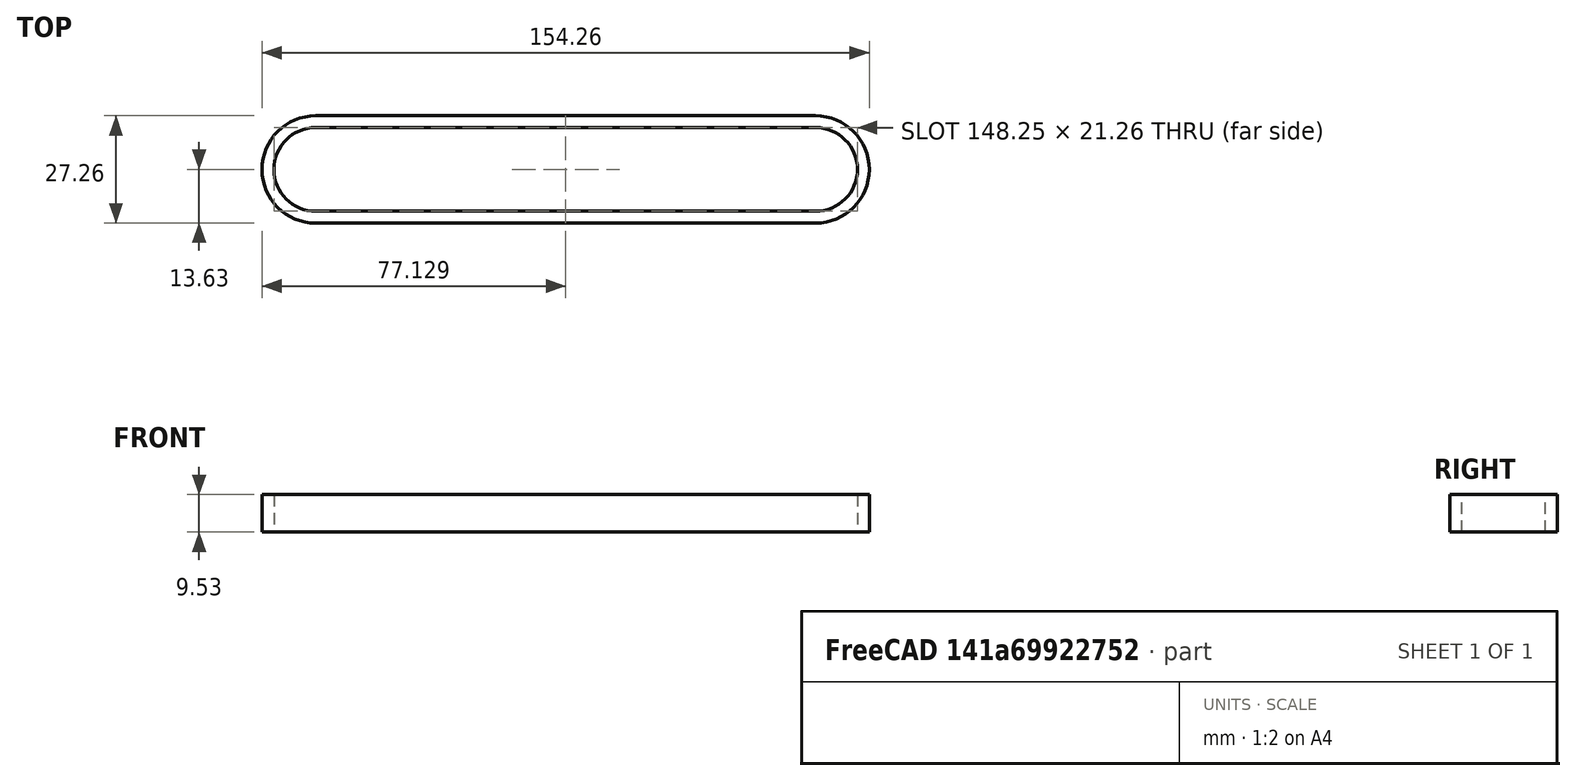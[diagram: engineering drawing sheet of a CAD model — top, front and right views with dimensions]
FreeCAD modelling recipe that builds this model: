
FCSTD DOCUMENT  (FreeCAD 0.19R22665 (Git))
Label: BELT-XL-130-375
License: All rights reserved
LicenseURL: http://en.wikipedia.org/wiki/All_rights_reserved
objects: Sketcher::SketchObject×1, PartDesign::Pad×1, PartDesign::CoordinateSystem×1, PartDesign::Body×1
note: 5 computed .brp shape members not serialized (recipe doc carries the construction recipe); baked Part::Feature solids carry a one-line shape summary decoded from their .brp

FEATURE [Sketcher::SketchObject] Sketch
  MapMode = 5
  Support = -> [XY_Plane]
  expr: Constraints[7] = 25.4 * 0.955
  expr: Constraints[8] = (13 * 25.4 - 0.955 * 25.4 * pi) / 2
  sketch-geometry (12):
    g0: ArcOfCircle [constr] CenterX=0 CenterY=0 CenterZ=0 NormalX=0 NormalY=0 NormalZ=1 AngleXU=0 Radius=12.1285 StartAngle=1.5708 EndAngle=4.71239
    g1: ArcOfCircle [constr] CenterX=126.997 CenterY=-1e-16 CenterZ=0 NormalX=0 NormalY=0 NormalZ=1 AngleXU=0 Radius=12.1285 StartAngle=4.71239 EndAngle=7.85398
    g2: LineSegment [constr] StartX=0 StartY=-12.1285 StartZ=0 EndX=126.997 EndY=-12.1285 EndZ=0
    g3: LineSegment [constr] StartX=-1.5e-15 StartY=12.1285 StartZ=0 EndX=126.997 EndY=12.1285 EndZ=0
    g4: ArcOfCircle CenterX=0 CenterY=0 CenterZ=0 NormalX=0 NormalY=0 NormalZ=1 AngleXU=0 Radius=10.6285 StartAngle=1.5708 EndAngle=4.71239
    g5: ArcOfCircle CenterX=126.997 CenterY=-1e-16 CenterZ=0 NormalX=0 NormalY=0 NormalZ=1 AngleXU=0 Radius=10.6285 StartAngle=4.71239 EndAngle=7.85398
    g6: LineSegment StartX=0 StartY=-10.6285 StartZ=0 EndX=126.997 EndY=-10.6285 EndZ=0
    g7: LineSegment StartX=-1.7e-15 StartY=10.6285 StartZ=0 EndX=126.997 EndY=10.6285 EndZ=0
    g8: ArcOfCircle CenterX=0 CenterY=0 CenterZ=0 NormalX=0 NormalY=0 NormalZ=1 AngleXU=0 Radius=13.6285 StartAngle=1.5708 EndAngle=4.71239
    g9: ArcOfCircle CenterX=126.997 CenterY=-1e-16 CenterZ=0 NormalX=0 NormalY=0 NormalZ=1 AngleXU=0 Radius=13.6285 StartAngle=4.71239 EndAngle=7.85398
    g10: LineSegment StartX=2.759e-13 StartY=-13.6285 StartZ=0 EndX=126.997 EndY=-13.6285 EndZ=0
    g11: LineSegment StartX=-2.2515e-11 StartY=13.6285 StartZ=0 EndX=126.997 EndY=13.6285 EndZ=0
  constraints (25):
    c: Tangent(g0,g3)
    c: Tangent(g0,g2)
    c: Tangent(g2,g1)
    c: Tangent(g3,g1)
    c: Horizontal(g2)
    c: Equal(g0,g1)
    c: Coincident(g0,g-1)
    c: Diameter(g0) = 24.257
    c: DistanceX(g3,g3) = 126.997
    c: Tangent(g4,g7)
    c: Tangent(g4,g6)
    c: Tangent(g6,g5)
    c: Tangent(g7,g5)
    c: Horizontal(g6)
    c: Coincident(g4,g-1)
    c: Coincident(g1,g5)
    c: Tangent(g8,g11)
    c: Tangent(g8,g10)
    c: Tangent(g10,g9)
    c: Tangent(g11,g9)
    c: Horizontal(g10)
    c: Coincident(g8,g4)
    c: Coincident(g9,g5)
    c: DistanceY(g5,g1) = 1.5
    c: DistanceY(g1,g9) = 1.5
FEATURE [PartDesign::Pad] Pad
  Direction = (1,1,1)
  Length = 9.525
  Length2 = 100
  Profile = -> Sketch
  Type = 0
FEATURE [PartDesign::CoordinateSystem] LCS_1
  AttacherType = Attacher::AttachEngine3D
  MapMode = 11
  Placement = pos=(0,0,0) rot=(0,0,1;3.14159rad)
  Support = -> [Pad]
FEATURE [PartDesign::Body] Body  label="BELT-XL-130-375"
  Group = -> [Sketch,Pad,LCS_1]
  Origin = -> Origin
  Tip = -> Pad
